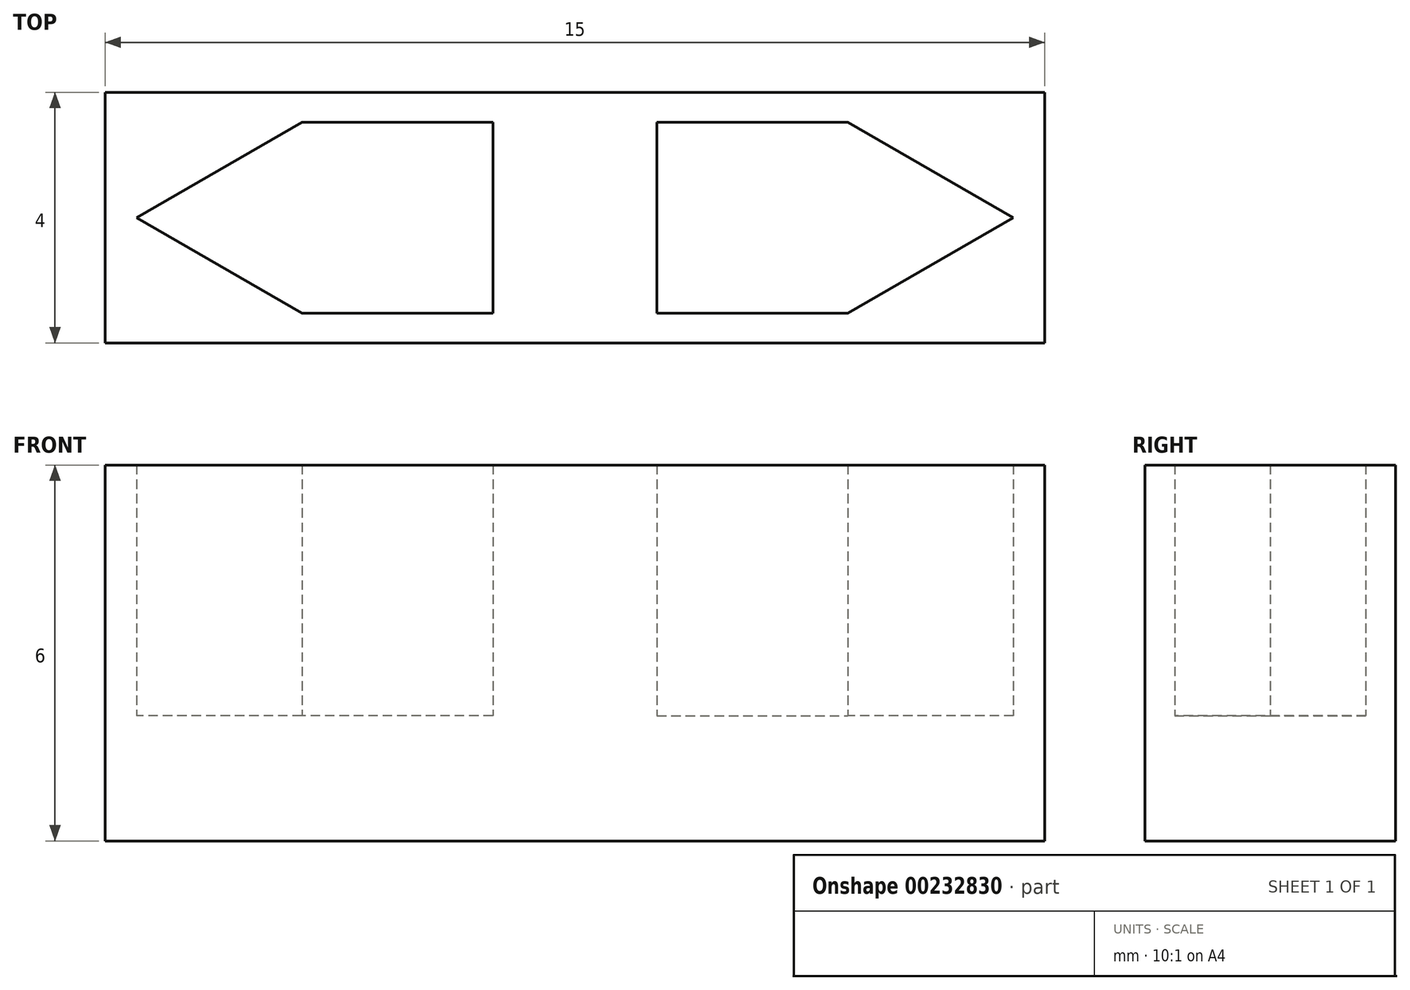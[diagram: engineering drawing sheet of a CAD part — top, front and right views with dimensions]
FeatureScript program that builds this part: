
annotation { "Feature Type Name" : "Feature", "Feature Type Description" : "" }
export const myFeature = defineFeature(function(context is Context, id is Id, definition is map)
    precondition{}
    {
        {
            var Q0;
            Q0=qCreatedBy(makeId("Top.planeOp"),FACE);
            var sketch = newSketch(context, id + "F0", { "sketchPlane" : qUnion([Q0])});
            skLineSegment(sketch, "E0.bottom", {"start": v(7.5, -2) * mm, "end": v(-7.5, -2) * mm});
            skLineSegment(sketch, "E0.top", {"start": v(7.5, 2) * mm, "end": v(-7.5, 2) * mm});
            skLineSegment(sketch, "E0.left", {"start": v(7.5, -2) * mm, "end": v(7.5, 2) * mm});
            skLineSegment(sketch, "E0.right", {"start": v(-7.5, -2) * mm, "end": v(-7.5, 2) * mm});
            skPoint(sketch, "E0.middle", {"position": v(0, 0) * mm});
            skLineSegment(sketch, "E1", {"start": v(-7, 0) * mm, "end": v(-4.36, 1.53) * mm});
            skLineSegment(sketch, "E2", {"start": v(-4.36, 1.53) * mm, "end": v(-4.36, -1.52) * mm});
            skLineSegment(sketch, "E3", {"start": v(-4.36, -1.52) * mm, "end": v(-7, 0) * mm});
            skLineSegment(sketch, "E4", {"start": v(7, 0) * mm, "end": v(4.36, 1.52) * mm});
            skLineSegment(sketch, "E5", {"start": v(4.36, 1.52) * mm, "end": v(4.36, -1.53) * mm});
            skLineSegment(sketch, "E6", {"start": v(4.36, -1.53) * mm, "end": v(7, 0) * mm});
            skSolve(sketch);
        }
        {
            var Q0;
            Q0=makeQuery(id+"F0.imprint","IMPRINT",FACE,{"disambiguationData":[TD([[makeQuery(id+"F0.imprint","IMPRINT",EDGE,{"derivedFrom":sQuery(id+"F0.wireOp",EDGE,"E0.bottom")}),-1.0]])]});
            extrude(context, id + "F1", {"entities" : qUnion([Q0]), "depth" : 4 * mm});
        }
        {
            var Q0;
            Q0=makeQuery(id+"F0.imprint","IMPRINT",FACE,{"disambiguationData":[TD([[makeQuery(id+"F0.imprint","IMPRINT",EDGE,{"derivedFrom":sQuery(id+"F0.wireOp",EDGE,"E1")}),-1.0]])]});
            var Q1;
            Q1=makeQuery(id+"F0.imprint","IMPRINT",FACE,{"disambiguationData":[TD([[makeQuery(id+"F0.imprint","IMPRINT",EDGE,{"derivedFrom":sQuery(id+"F0.wireOp",EDGE,"E0.bottom")}),-1.0]])]});
            var Q2;
            Q2=makeQuery(id+"F0.imprint","IMPRINT",FACE,{"disambiguationData":[TD([[makeQuery(id+"F0.imprint","IMPRINT",EDGE,{"derivedFrom":sQuery(id+"F0.wireOp",EDGE,"E4")}),1.0]])]});
            extrude(context, id + "F2", {"entities" : qUnion([Q0, Q1, Q2]), "operationType" : NewBodyOperationType.ADD, "oppositeDirection" : true, "depth" : 2 * mm});
        }
        {
            var Q0;
            Q0=makeQuery(id+"F1.opExtrude","SWEPT_FACE",FACE,{"disambiguationData":[OSD([sQuery(id+"F0.wireOp",EDGE,"E5")])]});
            extrude(context, id + "F3", {"entities" : qUnion([Q0]), "operationType" : NewBodyOperationType.REMOVE, "oppositeDirection" : true, "depth" : 3.05 * mm});
        }
        {
            var Q0;
            Q0=makeQuery(id+"F1.opExtrude","SWEPT_FACE",FACE,{"disambiguationData":[OSD([sQuery(id+"F0.wireOp",EDGE,"E2")])]});
            extrude(context, id + "F4", {"entities" : qUnion([Q0]), "operationType" : NewBodyOperationType.REMOVE, "oppositeDirection" : true, "depth" : 3.05 * mm});
        }
    });
